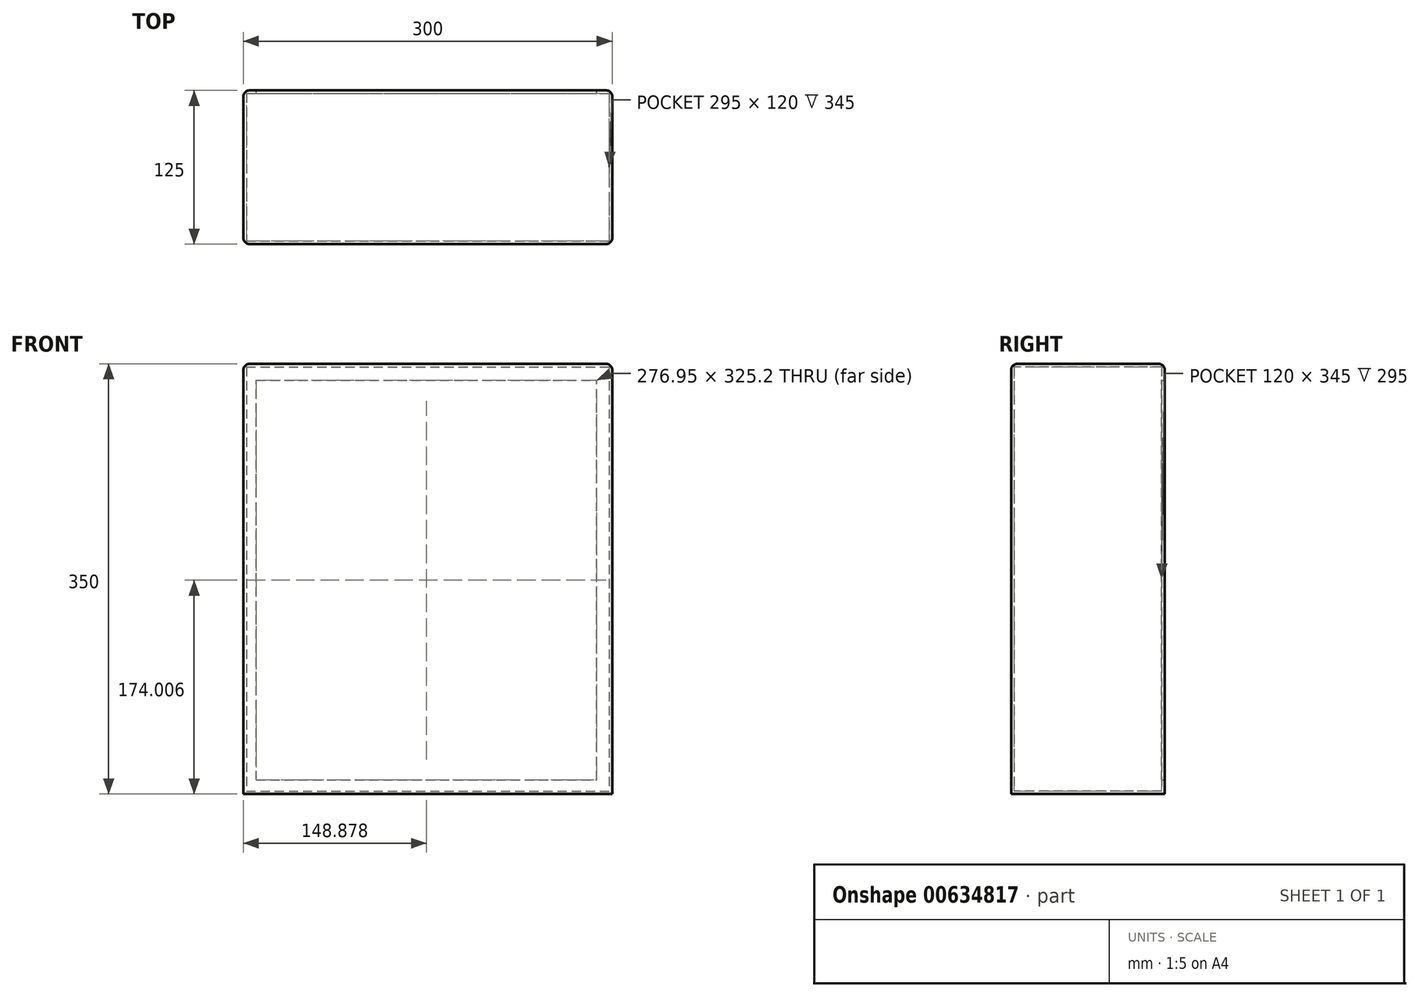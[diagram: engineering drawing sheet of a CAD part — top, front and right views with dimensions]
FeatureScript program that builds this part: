
annotation { "Feature Type Name" : "Feature", "Feature Type Description" : "" }
export const myFeature = defineFeature(function(context is Context, id is Id, definition is map)
    precondition{}
    {
        {
            var Q0;
            Q0=qCreatedBy(makeId("Front.planeOp"),FACE);
            var sketch = newSketch(context, id + "F0", { "sketchPlane" : qUnion([Q0])});
            skLineSegment(sketch, "E0.bottom", {"start": v(-54.25, 274.5) * mm, "end": v(245.75, 274.5) * mm});
            skLineSegment(sketch, "E0.top", {"start": v(-54.25, -75.5) * mm, "end": v(245.75, -75.5) * mm});
            skLineSegment(sketch, "E0.left", {"start": v(-54.25, 274.5) * mm, "end": v(-54.25, -75.5) * mm});
            skLineSegment(sketch, "E0.right", {"start": v(245.75, 274.5) * mm, "end": v(245.75, -75.5) * mm});
            skSolve(sketch);
        }
        {
            var Q0;
            Q0 = qSketchRegion(id + "F0", true);
            extrude(context, id + "F1", {"entities" : qUnion([Q0]), "oppositeDirection" : true, "depth" : 125 * mm, "offsetDistance" : 25 * mm});
        }
        {
            var Q0;
            Q0=makeQuery(id+"F1.opExtrude","CAP_FACE",FACE,{"disambiguationData":[OSD([sQuery(id+"F0.wireOp",EDGE,"E0.bottom"),sQuery(id+"F0.wireOp",EDGE,"E0.top"),sQuery(id+"F0.wireOp",EDGE,"E0.left"),sQuery(id+"F0.wireOp",EDGE,"E0.right")])],"isStart":true});
            var Q1;
            Q1=makeQuery(id+"F1.opExtrude","SWEPT_BODY",BODY,{"disambiguationData":[OSD([sQuery(id+"F0.wireOp",EDGE,"E0.bottom"),sQuery(id+"F0.wireOp",EDGE,"E0.top"),sQuery(id+"F0.wireOp",EDGE,"E0.left"),sQuery(id+"F0.wireOp",EDGE,"E0.right")])]});
            shell(context, id + "F2", {"isHollow" : true, "entities" : qUnion([Q0]), "parts" : qUnion([Q1]), "thickness" : 2.5 * mm});
        }
        {
            var Q0;
            Q0=makeQuery(id+"F1.opExtrude","SWEPT_EDGE",EDGE,{"disambiguationData":[OSD([sQuery(id+"F0.wireOp",EDGE,"E0.bottom"),sQuery(id+"F0.wireOp",EDGE,"E0.right")])]});
            var Q1;
            Q1=makeQuery(id+"F1.opExtrude","CAP_EDGE",EDGE,{"disambiguationData":[OSD([sQuery(id+"F0.wireOp",EDGE,"E0.bottom")])],"isStart":false});
            var Q2;
            Q2=makeQuery(id+"F1.opExtrude","CAP_EDGE",EDGE,{"disambiguationData":[OSD([sQuery(id+"F0.wireOp",EDGE,"E0.right")])],"isStart":false});
            var Q3;
            Q3=makeQuery(id+"F1.opExtrude","CAP_EDGE",EDGE,{"disambiguationData":[OSD([sQuery(id+"F0.wireOp",EDGE,"E0.left")])],"isStart":false});
            var Q4;
            Q4=makeQuery(id+"F1.opExtrude","SWEPT_EDGE",EDGE,{"disambiguationData":[OSD([sQuery(id+"F0.wireOp",EDGE,"E0.bottom"),sQuery(id+"F0.wireOp",EDGE,"E0.left")])]});
            var Q5;
            Q5=makeQuery(id+"F1.opExtrude","CAP_EDGE",EDGE,{"disambiguationData":[OSD([sQuery(id+"F0.wireOp",EDGE,"E0.bottom")])],"isStart":true});
            var Q6;
            Q6=makeQuery(id+"F1.opExtrude","CAP_EDGE",EDGE,{"disambiguationData":[OSD([sQuery(id+"F0.wireOp",EDGE,"E0.right")])],"isStart":true});
            var Q7;
            Q7=makeQuery(id+"F1.opExtrude","CAP_EDGE",EDGE,{"disambiguationData":[OSD([sQuery(id+"F0.wireOp",EDGE,"E0.left")])],"isStart":true});
            fillet(context, id + "F3", {"entities" : qUnion([Q0, Q1, Q2, Q3, Q4, Q5, Q6, Q7]), "radius" : 5 * mm, "tangentPropagation" : true, "allowEdgeOverflow" : false});
        }
        {
            var Q0;
            Q0=makeQuery(id+"F1.opExtrude","CAP_FACE",FACE,{"disambiguationData":[OSD([sQuery(id+"F0.wireOp",EDGE,"E0.bottom"),sQuery(id+"F0.wireOp",EDGE,"E0.top"),sQuery(id+"F0.wireOp",EDGE,"E0.left"),sQuery(id+"F0.wireOp",EDGE,"E0.right")])],"isStart":false});
            var sketch = newSketch(context, id + "F4", { "sketchPlane" : qUnion([Q0])});
            skLineSegment(sketch, "E1.bottom", {"start": v(-233.1, 261.12) * mm, "end": v(43.85, 261.12) * mm});
            skLineSegment(sketch, "E1.top", {"start": v(-233.1, -64.08) * mm, "end": v(43.85, -64.08) * mm});
            skLineSegment(sketch, "E1.left", {"start": v(-233.1, 261.12) * mm, "end": v(-233.1, -64.08) * mm});
            skLineSegment(sketch, "E1.right", {"start": v(43.85, 261.12) * mm, "end": v(43.85, -64.08) * mm});
            skSolve(sketch);
        }
        {
            var Q0;
            Q0 = qSketchRegion(id + "F4", true);
            extrude(context, id + "F5", {"entities" : qUnion([Q0]), "operationType" : NewBodyOperationType.REMOVE, "oppositeDirection" : true, "depth" : 120 * mm, "offsetDistance" : 25 * mm});
        }
    });
